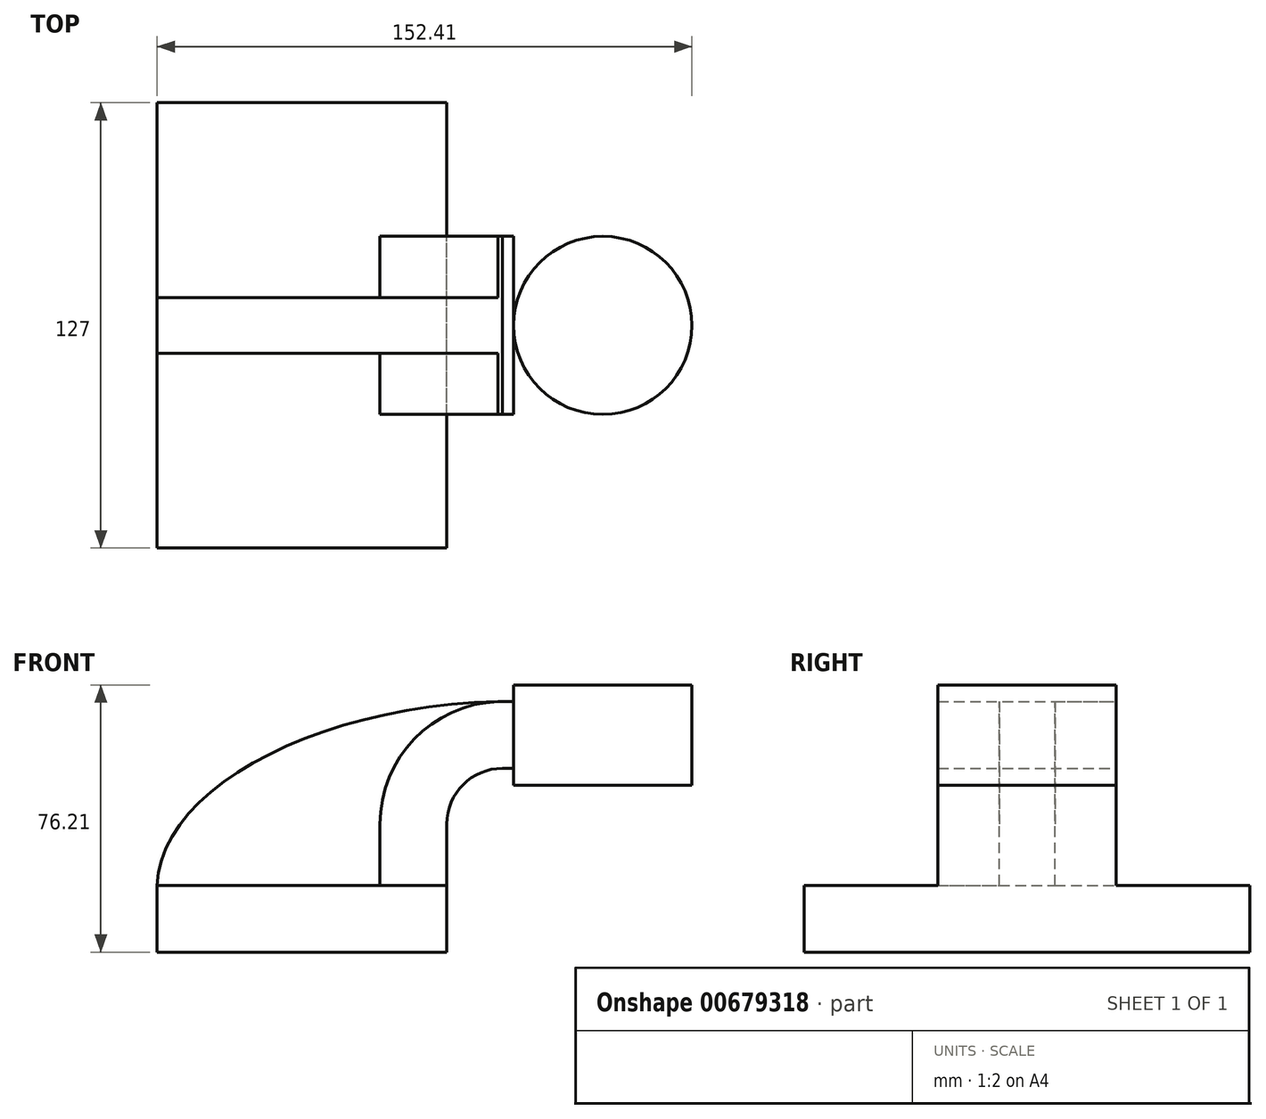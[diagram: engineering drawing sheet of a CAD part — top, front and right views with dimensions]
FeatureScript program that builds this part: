
annotation { "Feature Type Name" : "Feature", "Feature Type Description" : "" }
export const myFeature = defineFeature(function(context is Context, id is Id, definition is map)
    precondition{}
    {
        {
            var Q0;
            Q0=qCreatedBy(makeId("Front.planeOp"),FACE);
            var sketch = newSketch(context, id + "F0", { "sketchPlane" : qUnion([Q0])});
            skLineSegment(sketch, "E0.bottom", {"start": v(-41.27, -9.53) * mm, "end": v(41.28, -9.53) * mm});
            skLineSegment(sketch, "E0.top", {"start": v(-41.28, 9.52) * mm, "end": v(41.28, 9.52) * mm});
            skLineSegment(sketch, "E0.left", {"start": v(-41.28, -9.53) * mm, "end": v(-41.28, 9.52) * mm});
            skLineSegment(sketch, "E0.right", {"start": v(41.28, -9.53) * mm, "end": v(41.28, 9.52) * mm});
            skPoint(sketch, "E0.middle", {"position": v(0, 0) * mm});
            skLineSegment(sketch, "E1.bottom", {"start": v(60.32, 66.67) * mm, "end": v(111.12, 66.67) * mm});
            skLineSegment(sketch, "E1.top", {"start": v(60.33, 38.1) * mm, "end": v(111.12, 38.1) * mm});
            skLineSegment(sketch, "E1.left", {"start": v(60.32, 66.67) * mm, "end": v(60.32, 38.1) * mm});
            skLineSegment(sketch, "E1.right", {"start": v(111.12, 66.67) * mm, "end": v(111.12, 38.1) * mm});
            skPoint(sketch, "E1.middle", {"position": v(85.72, 52.39) * mm});
            skLineSegment(sketch, "E2", {"start": v(41.28, 9.52) * mm, "end": v(41.28, 27) * mm});
            skArc(sketch, "E3", {"start": v(41.27, 27) * mm, "mid": v(45.92, 38.23) * mm, "end": v(57.15, 42.88) * mm});
            skLineSegment(sketch, "E4", {"start": v(57.15, 42.88) * mm, "end": v(80.68, 42.88) * mm});
            skLineSegment(sketch, "E5.0", {"start": v(57.15, 61.93) * mm, "end": v(80.68, 61.93) * mm});
            skArc(sketch, "E5.1", {"start": v(22.22, 27) * mm, "mid": v(32.45, 51.7) * mm, "end": v(57.15, 61.93) * mm});
            skLineSegment(sketch, "E5.2", {"start": v(22.23, 9.52) * mm, "end": v(22.23, 27) * mm});
            skFitSpline(sketch, "E6", {"points": [v(-41.27, 9.53) * mm, v(57.15, 61.93) * mm], "startDerivative": vector(2.74, 83.66) * mm, "endDerivative": vector(156.2, 2.34) * mm});
            skLineSegment(sketch, "E7", {"start": v(85.72, 66.67) * mm, "end": v(85.72, 38.1) * mm});
            skLineSegment(sketch, "E8.0", {"start": v(66.68, 66.67) * mm, "end": v(66.68, 38.1) * mm});
            skSolve(sketch);
        }
        {
            var Q0;
            Q0=makeQuery(id+"F0.imprint","IMPRINT",FACE,{"disambiguationData":[TD([[makeQuery(id+"F0.imprint","IMPRINT",EDGE,{"derivedFrom":sQuery(id+"F0.wireOp",EDGE,"E0.bottom")}),1.0]])]});
            extrude(context, id + "F1", {"entities" : qUnion([Q0]), "endBound" : BoundingType.SYMMETRIC, "depth" : 127 * mm, "offsetDistance" : 25.4 * mm});
        }
        {
            var Q0;
            {var subQ0=sQuery(id+"F0.wireOp",EDGE,"E2");Q0=makeQuery(id+"F0.imprint","IMPRINT",FACE,{"disambiguationData":[TD([[makeQuery(id+"F0.imprint","IMPRINT",EDGE,{"derivedFrom":subQ0}),1.0]])]});}
            extrude(context, id + "F2", {"entities" : qUnion([Q0]), "operationType" : NewBodyOperationType.ADD, "endBound" : BoundingType.SYMMETRIC, "depth" : 50.8 * mm, "offsetDistance" : 25.4 * mm});
        }
        {
            var Q0;
            {var subQ3=sQuery(id+"F0.wireOp",EDGE,"E5.2");Q0=makeQuery(id+"F0.imprint","IMPRINT",FACE,{"disambiguationData":[TD([[makeQuery(id+"F0.imprint","IMPRINT",EDGE,{"derivedFrom":subQ3}),1.0]])]});}
            extrude(context, id + "F3", {"entities" : qUnion([Q0]), "operationType" : NewBodyOperationType.ADD, "endBound" : BoundingType.SYMMETRIC, "depth" : 15.88 * mm, "offsetDistance" : 25.4 * mm});
        }
        {
            var Q0;
            {var subQ0=sQuery(id+"F0.wireOp",EDGE,"E1.right");Q0=makeQuery(id+"F0.imprint","IMPRINT",FACE,{"disambiguationData":[TD([[makeQuery(id+"F0.imprint","IMPRINT",EDGE,{"derivedFrom":subQ0}),-1.0]])]});}
            var Q1;
            Q1=sQuery(id+"F0.wireOp",EDGE,"E7");
            revolve(context, id + "F4", {"operationType" : NewBodyOperationType.ADD, "entities" : qUnion([Q0]), "axis" : qUnion([Q1]), "revolveType" : RevolveType.FULL});
        }
    });
